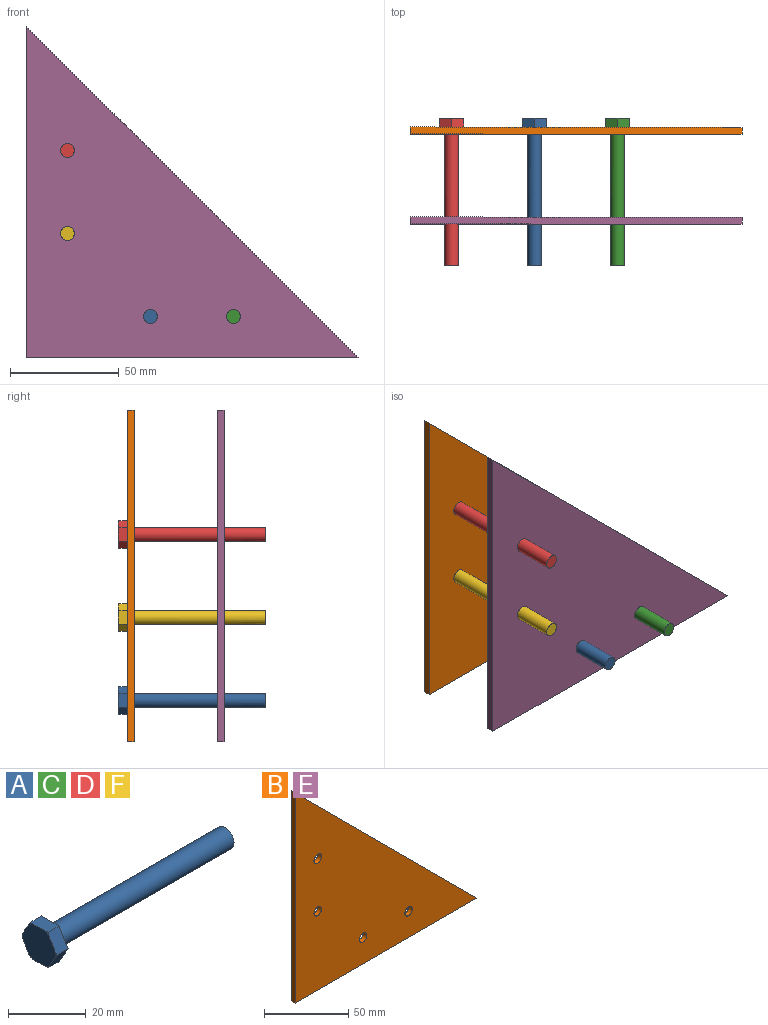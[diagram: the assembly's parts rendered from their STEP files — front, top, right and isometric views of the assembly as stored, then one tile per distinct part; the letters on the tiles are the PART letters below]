
ASSEMBLY  parts=6 mates=7
PART A: 16 faces, bbox 67.7x12.9x11.9 mm
  f0: plane 6.46x4.16mm, normal (0,0,1), area 26.2mm2, adj f1,f5,f6,f11,f13,f15
  f1: plane 5.6x4.16mm, normal (0,0.87,0.5), area 26.2mm2, adj f0,f2,f10,f11,f13,f15
  f2: plane 5.6x4.16mm, normal (0,0.87,-0.5), area 26.2mm2, adj f1,f3,f9,f10,f13,f15
  f3: plane 6.46x4.16mm, normal (0,0,-1), area 26.2mm2, adj f2,f4,f8,f9,f13,f15
  f4: plane 5.6x4.16mm, normal (0,-0.87,-0.5), area 26.2mm2, adj f3,f5,f7,f8,f13,f15
  f5: plane 5.6x4.16mm, normal (0,-0.87,0.5), area 26.2mm2, adj f0,f4,f6,f7,f13,f15
  f6: cone r=5.56mm half-angle=60deg, axis (1,0,0), area 0.4mm2, adj f0,f5,f15
  f7: cone r=5.56mm half-angle=60deg, axis (1,0,0), area 0.4mm2, adj f4,f5,f15
  f8: cone r=5.56mm half-angle=60deg, axis (1,0,0), area 0.4mm2, adj f3,f4,f15
  f9: cone r=5.56mm half-angle=60deg, axis (1,0,0), area 0.4mm2, adj f2,f3,f15
  f10: cone r=5.56mm half-angle=60deg, axis (1,0,0), area 0.4mm2, adj f1,f2,f15
  f11: cone r=5.56mm half-angle=60deg, axis (1,0,0), area 0.4mm2, adj f0,f1,f15
  f12: cylinder r=3.17mm len=63.5mm, axis (1,0,0), area 1266.8mm2, adj f13,f14
  f13: plane 12.83x11.11mm, normal (1,0,0), area 75.3mm2, adj f0,f1,f2,f3,f4,f5,f12
  f14: plane 6.35x6.35mm, normal (1,0,0), area 31.7mm2, adj f12
  f15: plane 12x11.12mm, normal (-1,0,0), area 105mm2, adj f0,f1,f2,f3,f4,f5,f6,f7
PART B: 9 faces, bbox 152.4x3.2x152.4 mm
  f0: plane 152.4x3.18mm, normal (0,0,-1), area 483.9mm2, adj f1,f2,f3,f4
  f1: plane 152.4x152.4mm, normal (0.71,0,0.71), area 684.3mm2, adj f0,f2,f3,f4
  f2: plane 152.4x3.18mm, normal (-1,0,0), area 483.9mm2, adj f0,f1,f3,f4
  f3: plane 152.4x152.4mm, normal (0,-1,0), area 11486.2mm2, adj f0,f1,f2,f5,f6,f7,f8
  f4: plane 152.4x152.4mm, normal (0,1,0), area 11486.2mm2, adj f0,f1,f2,f5,f6,f7,f8
  f5: cylinder r=3.17mm len=6.35mm, axis (0,1,0), area 63.3mm2, adj f3,f4
  f6: cylinder r=3.17mm len=6.35mm, axis (0,1,0), area 63.3mm2, adj f3,f4
  f7: cylinder r=3.17mm len=6.35mm, axis (0,1,0), area 63.3mm2, adj f3,f4
  f8: cylinder r=3.17mm len=6.35mm, axis (0,1,0), area 63.3mm2, adj f3,f4
PART C: same geometry as A
PART D: same geometry as A
PART E: same geometry as B
PART F: same geometry as A
PLACE A rot(axis=(0.58,-0.58,-0.58),120deg) t=(-102.4,-108.22,-58.84)mm
PLACE B t=(-159.55,-78.66,-77.89)mm
PLACE C rot(axis=(0.58,-0.58,-0.58),120deg) t=(-64.3,-108.22,-58.84)mm
PLACE D rot(axis=(0.58,-0.58,-0.58),120deg) t=(-140.5,-108.22,17.36)mm
PLACE E t=(-159.55,-119.93,-77.89)mm
PLACE F rot(axis=(0.58,-0.58,-0.58),120deg) t=(-140.5,-108.22,-20.74)mm
MATE fastened B.f5 <-> F.f6  axis (0,1,0) through (-140.5,-78.66,-20.74)mm
MATE fastened B.f6 <-> D.f6  axis (0,1,0) through (-140.5,-78.66,17.36)mm
MATE fastened B.f8 <-> C.f6  axis (0,1,0) through (-64.3,-78.66,-58.84)mm
MATE planar B.f3 <-> E.f7  axis (0,-1,0) through (-108.71,-81.83,-27.06)mm
MATE fastened B.f7 <-> A.f6  axis (0,1,0) through (-102.4,-78.66,-58.84)mm
MATE cylindrical E.f6 <-> D.f6  axis (0,1,0) through (-140.5,-123.11,17.36)mm
MATE cylindrical E.f8 <-> C.f6  axis (0,1,0) through (-64.3,-123.11,-58.84)mm
